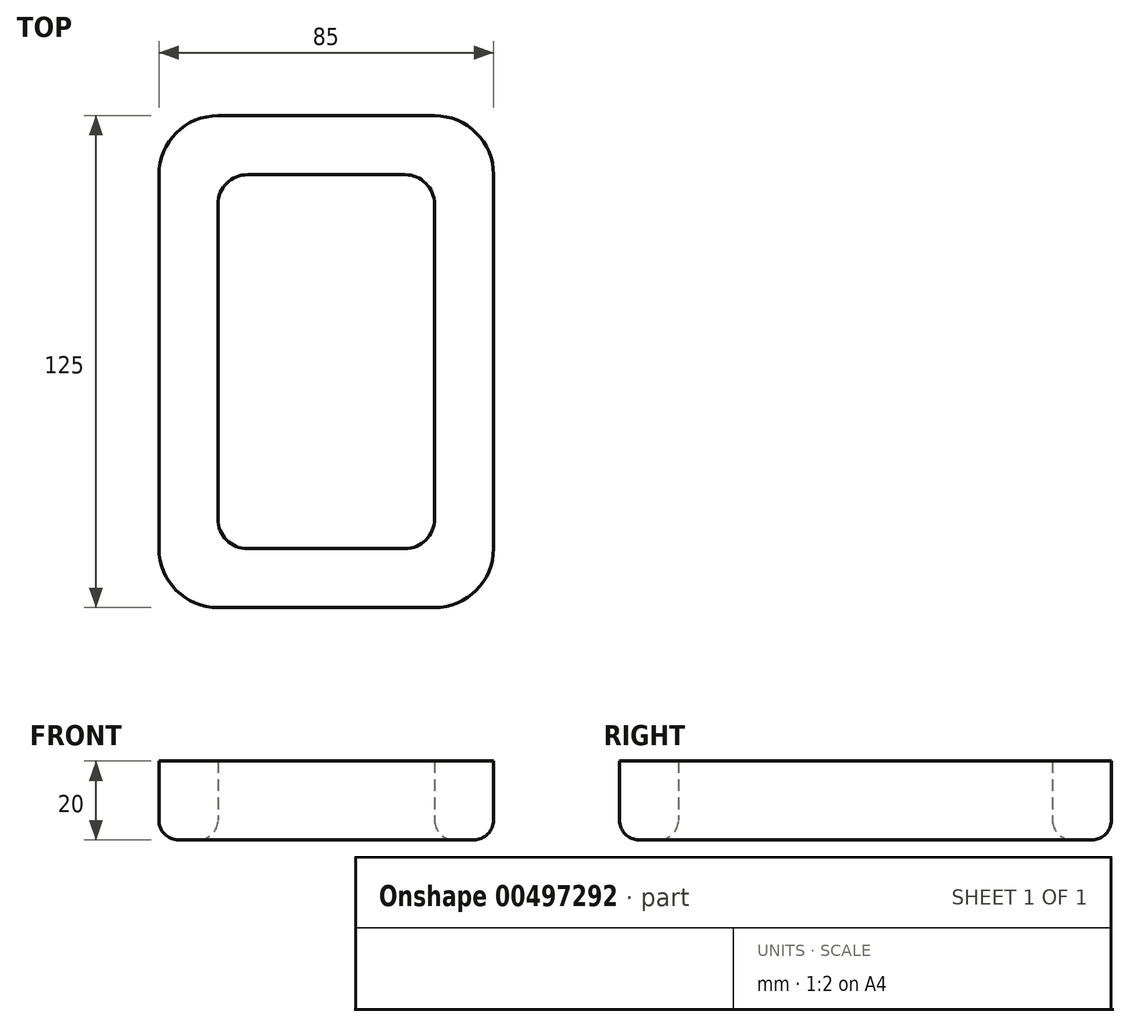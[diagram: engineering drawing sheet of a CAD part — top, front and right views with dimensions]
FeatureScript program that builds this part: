
annotation { "Feature Type Name" : "Feature", "Feature Type Description" : "" }
export const myFeature = defineFeature(function(context is Context, id is Id, definition is map)
    precondition{}
    {
        {
            var Q0;
            Q0=qCreatedBy(makeId("Top.planeOp"),FACE);
            var sketch = newSketch(context, id + "F0", { "sketchPlane" : qUnion([Q0])});
            skLineSegment(sketch, "E0.bottom", {"start": v(27.5, 62.5) * mm, "end": v(-27.5, 62.5) * mm});
            skLineSegment(sketch, "E0.top", {"start": v(27.5, -62.5) * mm, "end": v(-27.5, -62.5) * mm});
            skLineSegment(sketch, "E0.left", {"start": v(42.5, 47.5) * mm, "end": v(42.5, -47.5) * mm});
            skLineSegment(sketch, "E0.right", {"start": v(-42.5, 47.5) * mm, "end": v(-42.5, -47.5) * mm});
            skPoint(sketch, "E0.middle", {"position": v(0, 0) * mm});
            skLineSegment(sketch, "E1.0", {"start": v(20, 47.5) * mm, "end": v(-20, 47.5) * mm});
            skLineSegment(sketch, "E1.1", {"start": v(27.5, 40) * mm, "end": v(27.5, -40) * mm});
            skLineSegment(sketch, "E1.2", {"start": v(20, -47.5) * mm, "end": v(-20, -47.5) * mm});
            skLineSegment(sketch, "E1.3", {"start": v(-27.5, 40) * mm, "end": v(-27.5, -40) * mm});
            skPoint(sketch, "E2.visualSharp", {"position": v(-27.5, 47.5) * mm});
            skArc(sketch, "E2.filletArc", {"start": v(-20, 47.5) * mm, "mid": v(-25.3, 45.3) * mm, "end": v(-27.5, 40) * mm});
            skPoint(sketch, "E3.visualSharp", {"position": v(27.5, 47.5) * mm});
            skArc(sketch, "E3.filletArc", {"start": v(27.5, 40) * mm, "mid": v(25.3, 45.3) * mm, "end": v(20, 47.5) * mm});
            skPoint(sketch, "E4.visualSharp", {"position": v(27.5, -47.5) * mm});
            skArc(sketch, "E4.filletArc", {"start": v(20, -47.5) * mm, "mid": v(25.3, -45.3) * mm, "end": v(27.5, -40) * mm});
            skPoint(sketch, "E5.visualSharp", {"position": v(-27.5, -47.5) * mm});
            skArc(sketch, "E5.filletArc", {"start": v(-27.5, -40) * mm, "mid": v(-25.3, -45.3) * mm, "end": v(-20, -47.5) * mm});
            skPoint(sketch, "E6.visualSharp", {"position": v(-42.5, 62.5) * mm});
            skArc(sketch, "E6.filletArc", {"start": v(-27.5, 62.5) * mm, "mid": v(-38.1, 58.1) * mm, "end": v(-42.5, 47.5) * mm});
            skPoint(sketch, "E7.visualSharp", {"position": v(42.5, 62.5) * mm});
            skArc(sketch, "E7.filletArc", {"start": v(42.5, 47.5) * mm, "mid": v(38.1, 58.1) * mm, "end": v(27.5, 62.5) * mm});
            skPoint(sketch, "E8.visualSharp", {"position": v(42.5, -62.5) * mm});
            skArc(sketch, "E8.filletArc", {"start": v(27.5, -62.5) * mm, "mid": v(38.1, -58.1) * mm, "end": v(42.5, -47.5) * mm});
            skPoint(sketch, "E9.visualSharp", {"position": v(-42.5, -62.5) * mm});
            skArc(sketch, "E9.filletArc", {"start": v(-42.5, -47.5) * mm, "mid": v(-38.1, -58.1) * mm, "end": v(-27.5, -62.5) * mm});
            skSolve(sketch);
        }
        {
            var Q0;
            Q0=makeQuery(id+"F0.imprint","IMPRINT",FACE,{"disambiguationData":[TD([[makeQuery(id+"F0.imprint","IMPRINT",EDGE,{"derivedFrom":sQuery(id+"F0.wireOp",EDGE,"E0.bottom")}),1.0]])]});
            extrude(context, id + "F1", {"entities" : qUnion([Q0]), "depth" : 20 * mm});
        }
        {
            var Q0;
            Q0=makeQuery(id+"F1.opExtrude","CAP_FACE",FACE,{"disambiguationData":[OSD([sQuery(id+"F0.wireOp",EDGE,"E0.bottom"),sQuery(id+"F0.wireOp",EDGE,"E0.top"),sQuery(id+"F0.wireOp",EDGE,"E0.left"),sQuery(id+"F0.wireOp",EDGE,"E0.right"),sQuery(id+"F0.wireOp",EDGE,"E1.0"),sQuery(id+"F0.wireOp",EDGE,"E1.1"),sQuery(id+"F0.wireOp",EDGE,"E1.2"),sQuery(id+"F0.wireOp",EDGE,"E1.3"),sQuery(id+"F0.wireOp",EDGE,"E2.filletArc"),sQuery(id+"F0.wireOp",EDGE,"E3.filletArc"),sQuery(id+"F0.wireOp",EDGE,"E4.filletArc"),sQuery(id+"F0.wireOp",EDGE,"E5.filletArc"),sQuery(id+"F0.wireOp",EDGE,"E6.filletArc"),sQuery(id+"F0.wireOp",EDGE,"E7.filletArc"),sQuery(id+"F0.wireOp",EDGE,"E8.filletArc"),sQuery(id+"F0.wireOp",EDGE,"E9.filletArc")])],"isStart":true});
            fillet(context, id + "F2", {"entities" : qUnion([Q0]), "radius" : 5 * mm, "tangentPropagation" : true, "allowEdgeOverflow" : false});
        }
    });
